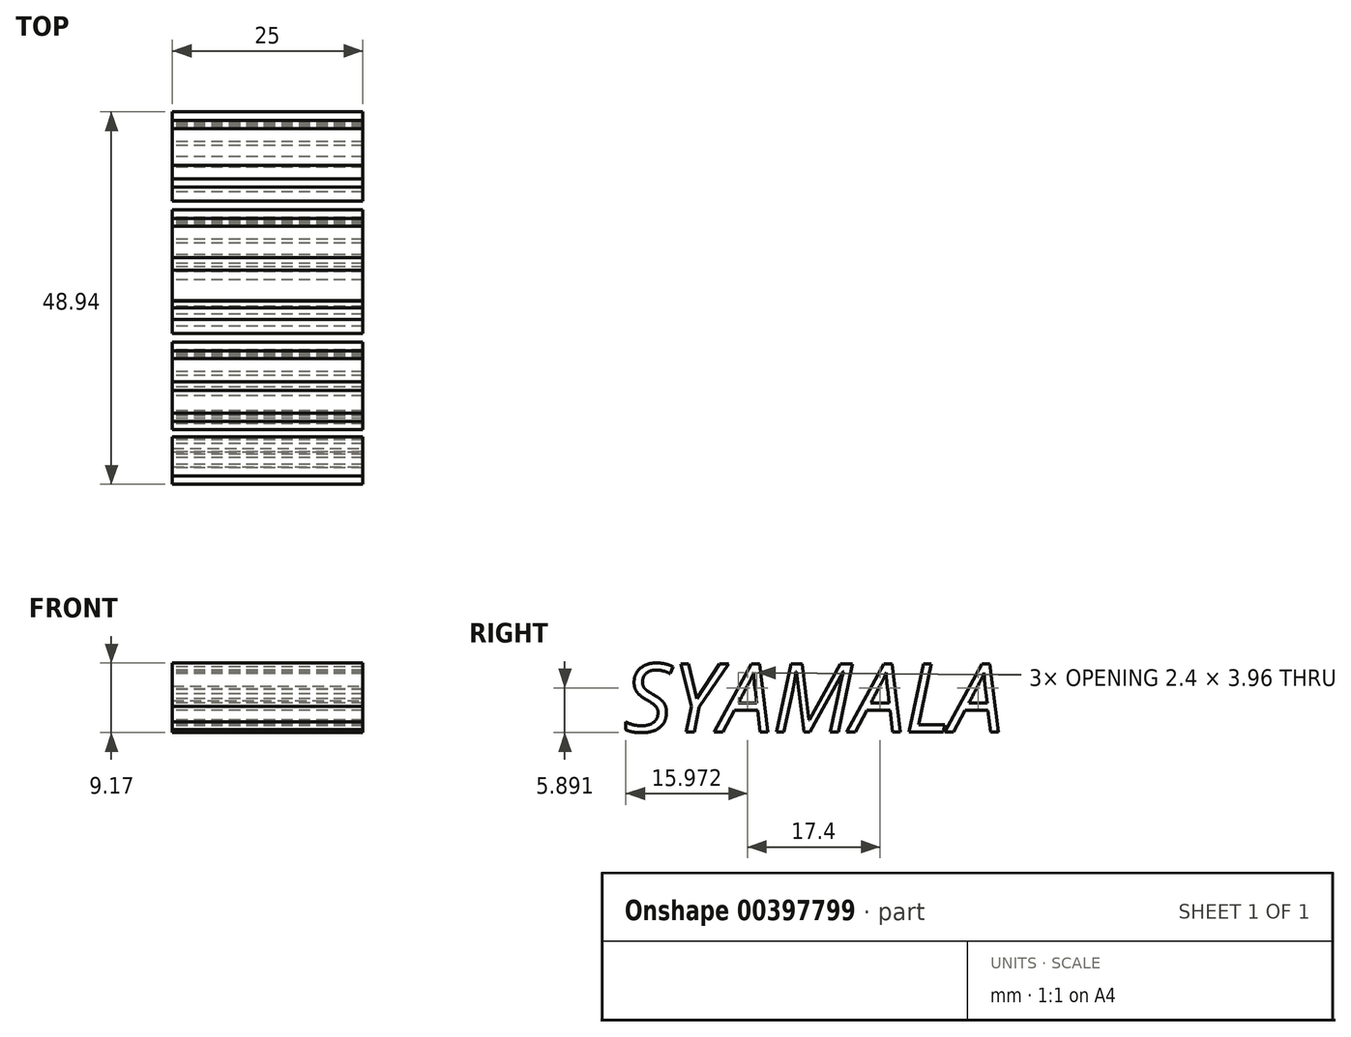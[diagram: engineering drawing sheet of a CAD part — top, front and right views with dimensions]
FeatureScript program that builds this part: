
annotation { "Feature Type Name" : "Feature", "Feature Type Description" : "" }
export const myFeature = defineFeature(function(context is Context, id is Id, definition is map)
    precondition{}
    {
        {
            var Q0;
            Q0=qCreatedBy(makeId("Right.planeOp"),FACE);
            var sketch = newSketch(context, id + "F0", { "sketchPlane" : qUnion([Q0])});
            skText(sketch, "E0", { "text": "SYAMALA", "fontName": "OpenSans-Italic.ttf"});
            const initialGuessF0  = {"E0": [-0.02755, -0.0064, 1, 0, 0.009]};
            skSetInitialGuess(sketch, initialGuessF0);
            skSolve(sketch);
        }
        {
            var Q0;
            Q0 = qSketchRegion(id + "F0", true);
            extrude(context, id + "F1", {"entities" : qUnion([Q0]), "depth" : 25 * mm});
        }
    });
